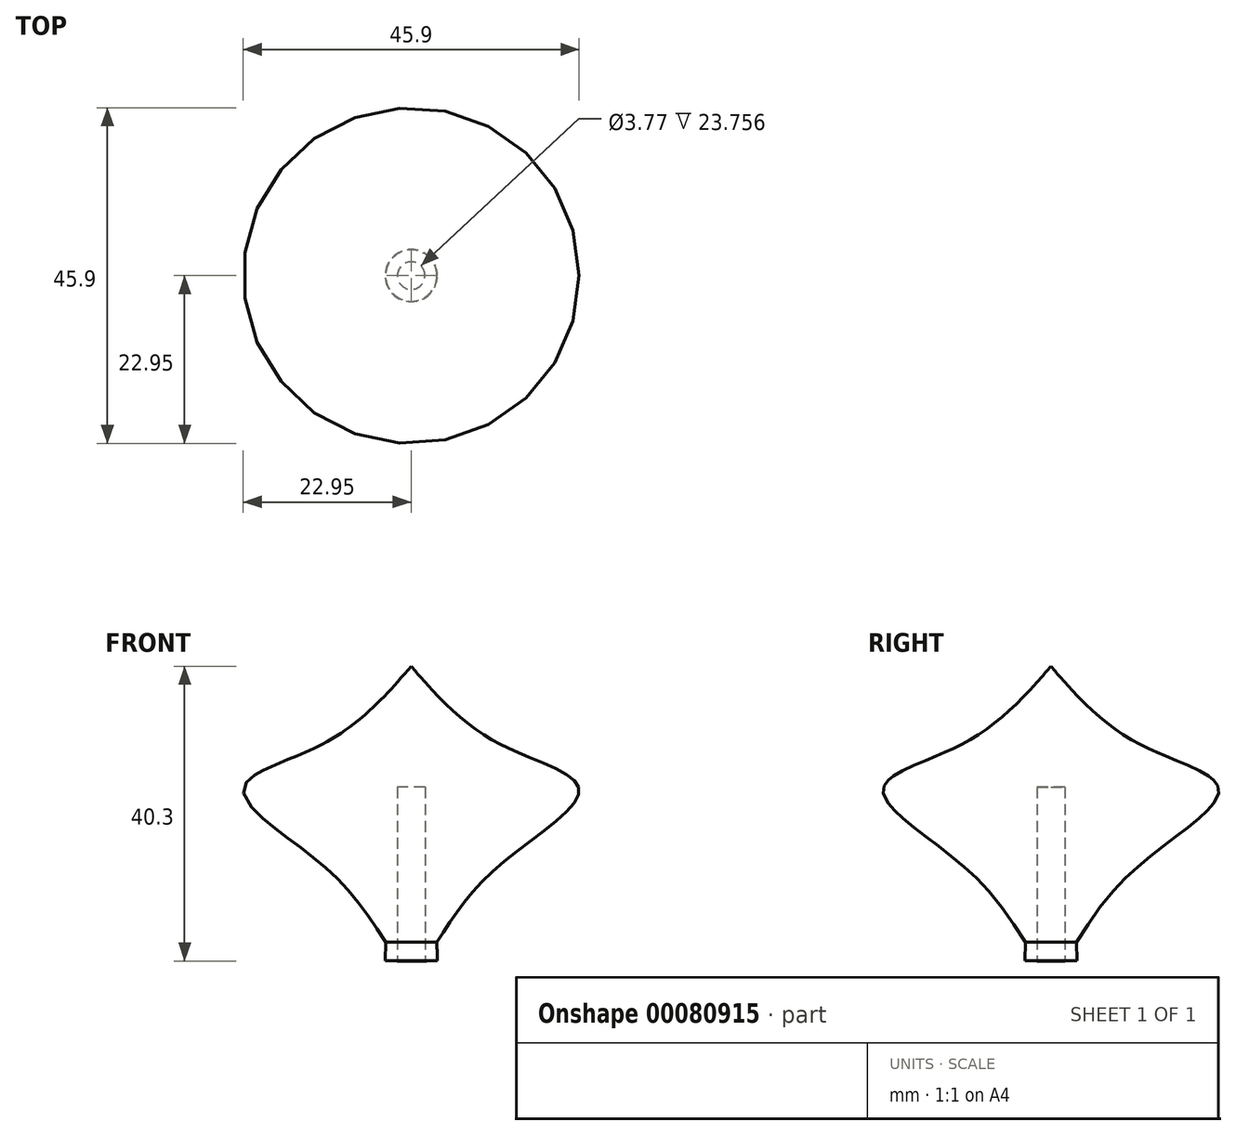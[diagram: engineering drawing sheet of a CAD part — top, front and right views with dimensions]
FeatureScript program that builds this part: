
annotation { "Feature Type Name" : "Feature", "Feature Type Description" : "" }
export const myFeature = defineFeature(function(context is Context, id is Id, definition is map)
    precondition{}
    {
        {
            var Q0;
            Q0=qCreatedBy(makeId("Front.planeOp"),FACE);
            var sketch = newSketch(context, id + "F0", { "sketchPlane" : qUnion([Q0])});
            skLineSegment(sketch, "E0", {"start": v(0, 26.1) * mm, "end": v(0, -3.85) * mm});
            skLineSegment(sketch, "E1", {"start": v(0, -15.55) * mm, "end": v(0, -3.85) * mm});
            skLineSegment(sketch, "E2", {"start": v(-3.14, 26.1) * mm, "end": v(-3.14, 36.9) * mm});
            skLineSegment(sketch, "E3", {"start": v(-3.14, 36.9) * mm, "end": v(0, 36.9) * mm});
            skLineSegment(sketch, "E4", {"start": v(0, 26.1) * mm, "end": v(0, 36.9) * mm});
            skLineSegment(sketch, "E5", {"start": v(0, -20.65) * mm, "end": v(0, -15.55) * mm});
            skLineSegment(sketch, "E6", {"start": v(0, 0) * mm, "end": v(0, -20.65) * mm});
            skArc(sketch, "E7", {"start": v(-12.19, 6.18) * mm, "mid": v(-7.37, 11.9) * mm, "end": v(-5.54, 19.14) * mm});
            skLineSegment(sketch, "E8", {"start": v(-3.14, 26.1) * mm, "end": v(-5.54, 26.1) * mm});
            skLineSegment(sketch, "E9", {"start": v(-5.54, 26.1) * mm, "end": v(-5.54, 19.14) * mm});
            skLineSegment(sketch, "E10", {"start": v(0, -20.65) * mm, "end": v(0, -25.1) * mm});
            skLineSegment(sketch, "E11", {"start": v(0, -25.1) * mm, "end": v(-1.89, -25.1) * mm});
            skLineSegment(sketch, "E12", {"start": v(-1.89, -25.1) * mm, "end": v(-1.89, -23.42) * mm});
            skLineSegment(sketch, "E13", {"start": v(-2.07, -23.42) * mm, "end": v(-3.56, -23.42) * mm});
            skLineSegment(sketch, "E14", {"start": v(-3.51, -20.9) * mm, "end": v(-3.56, -23.42) * mm});
            skLineSegment(sketch, "E15", {"start": v(-3.56, -23.42) * mm, "end": v(0, -23.5) * mm});
            skFitSpline(sketch, "E16", {"points": [v(0, 16.84) * mm, v(-12.19, 6.18) * mm, v(-22.95, 0) * mm, v(-12.19, -10.28) * mm, v(-3.51, -20.9) * mm], "startDerivative": vector(-39.13, -44.79) * mm, "endDerivative": vector(27.17, -42.9) * mm});
            skLineSegment(sketch, "E17", {"start": v(-5.54, 26.1) * mm, "end": v(0, 26.1) * mm});
            skSolve(sketch);
        }
        {
            var Q0;
            Q0=makeQuery(id+"F0.imprint","IMPRINT",FACE,{"disambiguationData":[TD([[makeQuery(id+"F0.imprint","IMPRINT",EDGE,{"derivedFrom":sQuery(id+"F0.wireOp",EDGE,"E2")}),-1.0]])]});
            var Q1;
            {var subQ0=sQuery(id+"F0.wireOp",EDGE,"E14");Q1=makeQuery(id+"F0.imprint","IMPRINT",FACE,{"disambiguationData":[TD([[makeQuery(id+"F0.imprint","IMPRINT",EDGE,{"derivedFrom":subQ0}),1.0]])]});}
            var Q2;
            {var subQ0=sQuery(id+"F0.wireOp",EDGE,"E11");Q2=makeQuery(id+"F0.imprint","IMPRINT",FACE,{"disambiguationData":[TD([[makeQuery(id+"F0.imprint","IMPRINT",EDGE,{"derivedFrom":subQ0}),-1.0]])]});}
            var Q3;
            Q3=sQuery(id+"F0.wireOp",EDGE,"E0");
            revolve(context, id + "F1", {"entities" : qUnion([Q0, Q1, Q2]), "axis" : qUnion([Q3]), "revolveType" : RevolveType.FULL});
        }
        {
            var Q0;
            Q0=makeQuery(id+"F1.opRevolve","SWEPT_FACE",FACE,{"disambiguationData":[OSD([sQuery(id+"F0.wireOp",EDGE,"E3")])]});
            extrude(context, id + "F2", {"entities" : qUnion([Q0]), "operationType" : NewBodyOperationType.REMOVE, "oppositeDirection" : true, "depth" : 18.8 * mm});
        }
        {
            var Q0;
            Q0=makeQuery(id+"F1.opRevolve","SWEPT_FACE",FACE,{"disambiguationData":[OSD([sQuery(id+"F0.wireOp",EDGE,"E11")])]});
            extrude(context, id + "F3", {"entities" : qUnion([Q0]), "operationType" : NewBodyOperationType.REMOVE, "oppositeDirection" : true, "depth" : 25.4 * mm});
        }
    });
